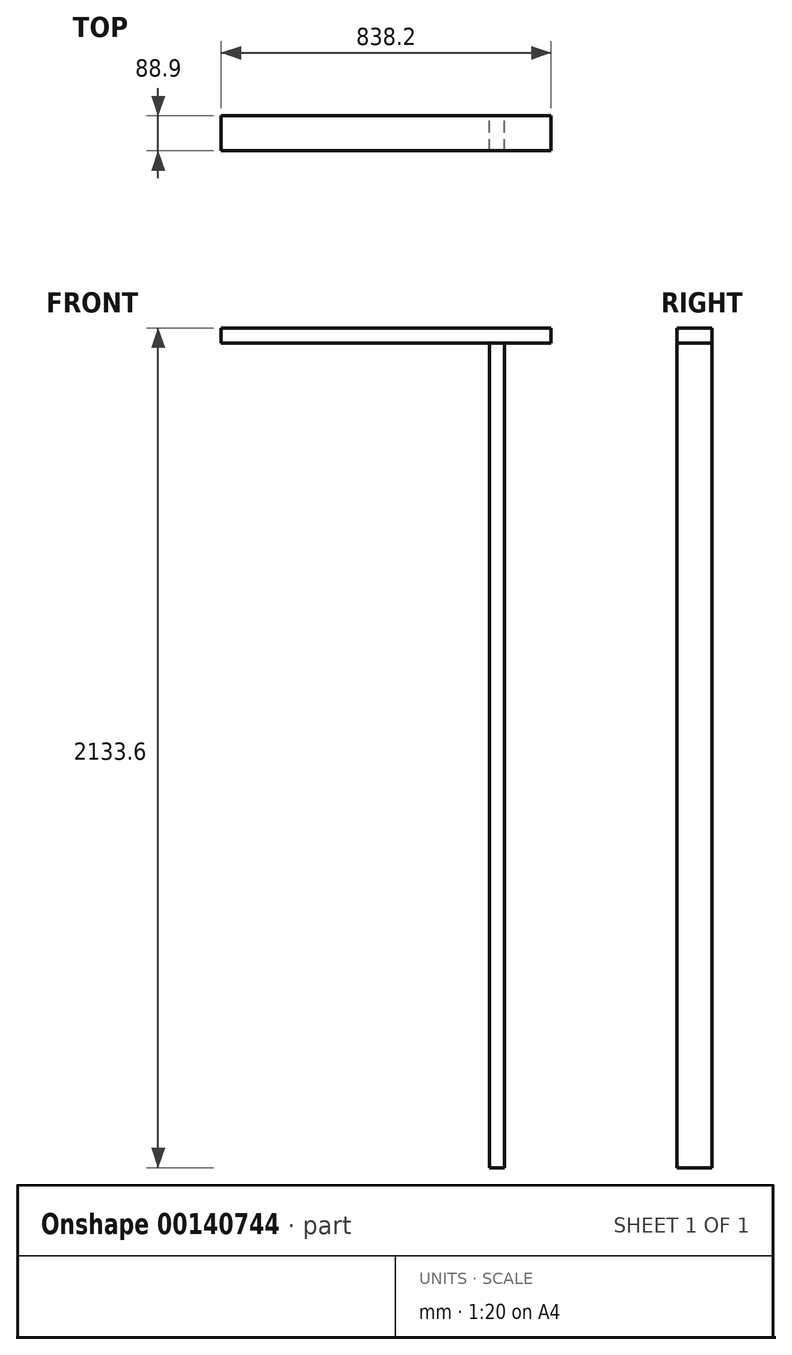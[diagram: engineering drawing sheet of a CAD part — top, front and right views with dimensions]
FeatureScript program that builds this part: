
annotation { "Feature Type Name" : "Feature", "Feature Type Description" : "" }
export const myFeature = defineFeature(function(context is Context, id is Id, definition is map)
    precondition{}
    {
        {
            var Q0;
            Q0=qCreatedBy(makeId("Right.planeOp"),FACE);
            var sketch = newSketch(context, id + "F0", { "sketchPlane" : qUnion([Q0])});
            skLineSegment(sketch, "E0.bottom", {"start": v(44.45, 19.05) * mm, "end": v(-44.45, 19.05) * mm});
            skLineSegment(sketch, "E0.top", {"start": v(44.45, -19.05) * mm, "end": v(-44.45, -19.05) * mm});
            skLineSegment(sketch, "E0.left", {"start": v(44.45, 19.05) * mm, "end": v(44.45, -19.05) * mm});
            skLineSegment(sketch, "E0.right", {"start": v(-44.45, 19.05) * mm, "end": v(-44.45, -19.05) * mm});
            skPoint(sketch, "E0.middle", {"position": v(0, 0) * mm});
            skSolve(sketch);
        }
        {
            var Q0;
            Q0 = qSketchRegion(id + "F0", true);
            extrude(context, id + "F1", {"entities" : qUnion([Q0]), "depth" : 838.2 * mm});
        }
        {
            var Q0;
            Q0=makeQuery(id+"F1.opExtrude","SWEPT_FACE",FACE,{"disambiguationData":[OSD([sQuery(id+"F0.wireOp",EDGE,"E0.top")])]});
            var sketch = newSketch(context, id + "F2", { "sketchPlane" : qUnion([Q0])});
            skLineSegment(sketch, "E1.bottom", {"start": v(720.08, 44.45) * mm, "end": v(681.98, 44.45) * mm});
            skLineSegment(sketch, "E1.top", {"start": v(720.08, -44.45) * mm, "end": v(681.98, -44.45) * mm});
            skLineSegment(sketch, "E1.left", {"start": v(720.08, 44.45) * mm, "end": v(720.08, -44.45) * mm});
            skLineSegment(sketch, "E1.right", {"start": v(681.98, 44.45) * mm, "end": v(681.98, -44.45) * mm});
            skSolve(sketch);
        }
        {
            var Q0;
            Q0 = qSketchRegion(id + "F2", true);
            extrude(context, id + "F3", {"entities" : qUnion([Q0]), "depth" : 2095.5 * mm});
        }
    });
